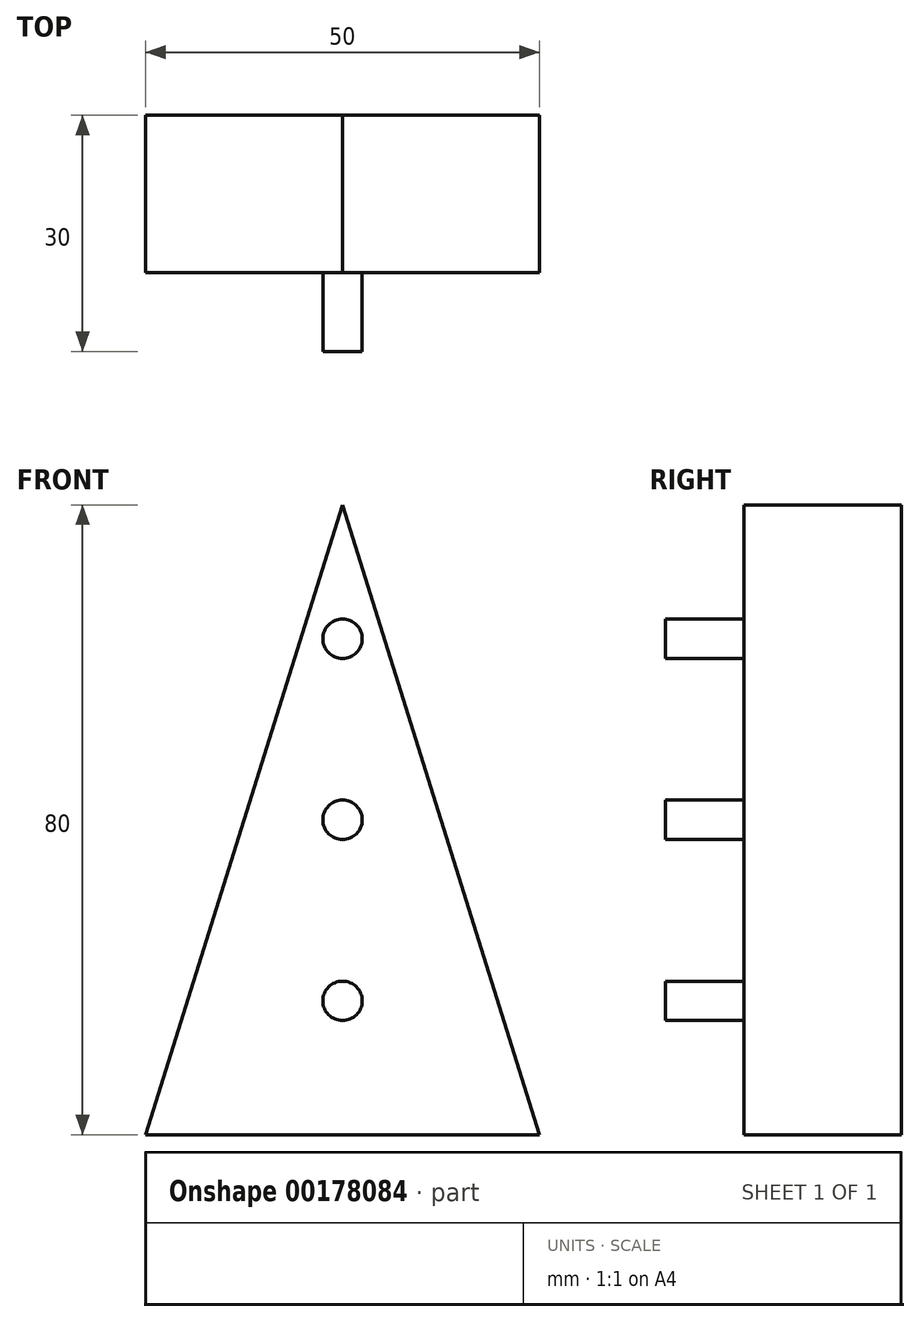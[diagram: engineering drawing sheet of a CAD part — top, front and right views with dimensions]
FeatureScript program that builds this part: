
annotation { "Feature Type Name" : "Feature", "Feature Type Description" : "" }
export const myFeature = defineFeature(function(context is Context, id is Id, definition is map)
    precondition{}
    {
        {
            var Q0;
            Q0=qCreatedBy(makeId("Front.planeOp"),FACE);
            var sketch = newSketch(context, id + "F0", { "sketchPlane" : qUnion([Q0])});
            skLineSegment(sketch, "E0", {"start": v(0, 40) * mm, "end": v(-25, -40) * mm});
            skLineSegment(sketch, "E1", {"start": v(-25, -40) * mm, "end": v(25, -40) * mm});
            skLineSegment(sketch, "E2", {"start": v(25, -40) * mm, "end": v(0, 40) * mm});
            skLineSegment(sketch, "E3", {"start": v(0, 40) * mm, "end": v(0, -40) * mm, "construction": true});
            skSolve(sketch);
        }
        {
            var Q0;
            Q0 = qSketchRegion(id + "F0", true);
            extrude(context, id + "F1", {"entities" : qUnion([Q0]), "oppositeDirection" : true, "depth" : 20 * mm});
        }
        {
            var Q0;
            Q0=qCreatedBy(makeId("Front.planeOp"),FACE);
            var sketch = newSketch(context, id + "F2", { "sketchPlane" : qUnion([Q0])});
            skCircle(sketch, "E4", {"center": v(0, 23) * mm, "radius": 2.5 * mm});
            skCircle(sketch, "E5", {"center": v(0, 0) * mm, "radius": 2.5 * mm});
            skCircle(sketch, "E6", {"center": v(0, -23) * mm, "radius": 2.5 * mm});
            skSolve(sketch);
        }
        {
            var Q0;
            Q0 = qSketchRegion(id + "F2", true);
            extrude(context, id + "F3", {"entities" : qUnion([Q0]), "operationType" : NewBodyOperationType.ADD, "depth" : 10 * mm});
        }
    });
